FCSTD DOCUMENT  (FreeCAD 0.15R4671 (Git))
Label: Robot1c
License: All rights reserved
LicenseURL: http://en.wikipedia.org/wiki/All_rights_reserved
objects: Part::Part2DObjectPython×50, App::DocumentObjectGroup×10, Part::Feature×1
note: 51 computed .brp shape members not serialized (recipe doc carries the construction recipe); baked Part::Feature solids carry a one-line shape summary decoded from their .brp

FEATURE [Part::Part2DObjectPython] BSpline  label="BSpline Top"  # Draft 2D object (typed FeaturePython)
  Closed = false
  MakeFace = true
  Placement = pos=(0,20,0) rot=(0,0,1;0rad)
  Points = (3) [(-50,50,0),(0,60,0),(50,50,0)]
FEATURE [Part::Part2DObjectPython] BSpline001  label="BSpline Bottom"  # Draft 2D object (typed FeaturePython)
  Closed = false
  MakeFace = true
  Placement = pos=(0,-20,0) rot=(0,0,1;0rad)
  Points = (3) [(-50,-50,0),(0,-60,0),(50,-50,0)]
FEATURE [Part::Part2DObjectPython] Line  label="Line Left"  # Draft 2D object (typed FeaturePython)
  ChamferSize = 0
  Closed = false
  End = (-50,-70,0)
  FilletRadius = 0
  Length = 140
  MakeFace = false
  Points = (2) [(-50,70,0),(-50,-70,0)]
  Start = (-50,70,0)
FEATURE [Part::Part2DObjectPython] Line001  label="Line Right"  # Draft 2D object (typed FeaturePython)
  ChamferSize = 0
  Closed = false
  End = (50,-70,0)
  FilletRadius = 0
  Length = 140
  MakeFace = false
  Points = (2) [(50,70,0),(50,-70,0)]
  Start = (50,70,0)
FEATURE [Part::Part2DObjectPython] Circle  label="Upper Hole NW"  # Draft 2D object (typed FeaturePython)
  FirstAngle = 0
  LastAngle = 0
  MakeFace = false
  Placement = pos=(-80,57,0) rot=(0,0,1;0rad)
  Radius = 1.5
FEATURE [Part::Part2DObjectPython] Circle001  label="Lower Hole NW"  # Draft 2D object (typed FeaturePython)
  FirstAngle = 0
  LastAngle = 0
  MakeFace = false
  Placement = pos=(-80,40,0) rot=(0,0,1;0rad)
  Radius = 1.5
FEATURE [Part::Part2DObjectPython] Circle002  label="Upper Hole NE"  # Draft 2D object (typed FeaturePython)
  FirstAngle = 0
  LastAngle = 0
  MakeFace = false
  Placement = pos=(80,57,0) rot=(0,0,1;0rad)
  Radius = 1.5
FEATURE [Part::Part2DObjectPython] Circle003  label="Lower Hole NE"  # Draft 2D object (typed FeaturePython)
  FirstAngle = 0
  LastAngle = 0
  MakeFace = false
  Placement = pos=(80,40,0) rot=(0,0,1;0rad)
  Radius = 1.5
FEATURE [Part::Part2DObjectPython] DWire  label="Bracket Line NE"  # Draft 2D object (typed FeaturePython)
  ChamferSize = 0
  Closed = true
  End = (65,68,0)
  FilletRadius = 0
  Length = 123.985
  MakeFace = false
  Placement = pos=(145,2,0) rot=(0,0,1;0rad)
  Points = (8) [(-79.946,60.961,0),(-71,61,0),(-71,34,0),(-59,34,0),(-59,61,0),(-50,61,0),(-50,66,0),(-80,66,0)]
  Start = (65.054,62.961,0)
FEATURE [Part::Part2DObjectPython] Circle004  label="Upper Hole SW"  # Draft 2D object (typed FeaturePython)
  FirstAngle = 0
  LastAngle = 0
  MakeFace = false
  Placement = pos=(-60,-72,0) rot=(0,0,1;3.14159rad)
  Radius = 1.5
FEATURE [Part::Part2DObjectPython] Circle005  label="Lower Hole SW"  # Draft 2D object (typed FeaturePython)
  FirstAngle = 0
  LastAngle = 0
  MakeFace = false
  Placement = pos=(-60,-55,0) rot=(0,0,1;3.14159rad)
  Radius = 1.5
FEATURE [Part::Part2DObjectPython] DWire002  label="Bracket Line SW"  # Draft 2D object (typed FeaturePython)
  ChamferSize = 0
  Closed = true
  End = (-45,-83,0)
  FilletRadius = 0
  Length = 124
  MakeFace = false
  Placement = pos=(-125,-17,0) rot=(0,0,1;3.14159rad)
  Points = (8) [(-80,61,0),(-71,61,0),(-71,34,0),(-59,34,0),(-59,61,0),(-50,61,0),(-50,66,0),(-80,66,0)]
  Start = (-45,-78,0)
FEATURE [Part::Part2DObjectPython] Circle006  label="Upper Hole SE"  # Draft 2D object (typed FeaturePython)
  FirstAngle = 0
  LastAngle = 0
  MakeFace = false
  Placement = pos=(60,-72,0) rot=(0,0,1;3.14159rad)
  Radius = 1.5
FEATURE [Part::Part2DObjectPython] Circle007  label="Lower Hole SE"  # Draft 2D object (typed FeaturePython)
  FirstAngle = 0
  LastAngle = 0
  MakeFace = false
  Placement = pos=(60,-55,0) rot=(0,0,1;3.14159rad)
  Radius = 1.5
FEATURE [Part::Part2DObjectPython] DWire003  label="Bracket Line SE"  # Draft 2D object (typed FeaturePython)
  ChamferSize = 0
  Closed = true
  End = (75,-83,0)
  FilletRadius = 0
  Length = 124
  MakeFace = false
  Placement = pos=(-5,-17,0) rot=(0,0,1;3.14159rad)
  Points = (8) [(-80,61,0),(-71,61,0),(-71,34,0),(-59,34,0),(-59,61,0),(-50,61,0),(-50,66,0),(-80,66,0)]
  Start = (75,-78,0)
FEATURE [Part::Part2DObjectPython] Rectangle  label="Left Edge"  # Draft 2D object (typed FeaturePython)
  ChamferSize = 0
  FilletRadius = 0
  Height = -12
  Length = 3
  MakeFace = false
  Placement = pos=(-50,0,0) rot=(0,0,1;0rad)
FEATURE [Part::Part2DObjectPython] Rectangle001  label="Right Edge"  # Draft 2D object (typed FeaturePython)
  ChamferSize = 0
  FilletRadius = 0
  Height = -12
  Length = 3
  MakeFace = false
  Placement = pos=(47,0,0) rot=(0,0,1;0rad)
FEATURE [Part::Part2DObjectPython] Rectangle002  label="Left Inner Slot"  # Draft 2D object (typed FeaturePython)
  ChamferSize = 0
  FilletRadius = 0
  Height = -12
  Length = 3
  MakeFace = false
  Placement = pos=(-28,0,0) rot=(0,0,1;0rad)
FEATURE [Part::Part2DObjectPython] Rectangle003  label="Right Inner Slot"  # Draft 2D object (typed FeaturePython)
  ChamferSize = 0
  FilletRadius = 0
  Height = -12
  Length = 3
  MakeFace = false
  Placement = pos=(25.1317,0.340284,0) rot=(0,0,1;0rad)
FEATURE [Part::Part2DObjectPython] Circle008  label="Rim"  # Draft 2D object (typed FeaturePython)
  FirstAngle = 0
  LastAngle = 0
  MakeFace = false
  Placement = pos=(-85,0,0) rot=(0,0,1;0rad)
  Radius = 30
FEATURE [App::DocumentObjectGroup] Group001  label="Bracket SE"
  Group = -> [Circle006,Circle007,DWire003]
FEATURE [App::DocumentObjectGroup] Group002  label="Bracket SW"
  Group = -> [Circle004,Circle005,DWire002]
FEATURE [Part::Part2DObjectPython] Rectangle004  label="Axle hole"  # Draft 2D object (typed FeaturePython)
  ChamferSize = 0
  FilletRadius = 0
  Height = 3.5
  Length = 5.5
  MakeFace = false
  Placement = pos=(-87.75,-1.75,0) rot=(0,0,1;0rad)
FEATURE [Part::Part2DObjectPython] DWire004  label="Spoke Right"  # Draft 2D object (typed FeaturePython)
  ChamferSize = 0
  Closed = true
  End = (-76,2,0)
  FilletRadius = 0
  Length = 52.8444
  MakeFace = false
  Points = (4) [(-76,-2,0),(-64,-10,0),(-64,10,0),(-76,2,0)]
  Start = (-76,-2,0)
FEATURE [Part::Part2DObjectPython] DWire005  label="Spoke Bottom"  # Draft 2D object (typed FeaturePython)
  ChamferSize = 0
  Closed = true
  End = (-83,-7,0)
  FilletRadius = 0
  Length = 52.8444
  MakeFace = false
  Placement = pos=(-85,-83,0) rot=(0,0,-1;1.5708rad)
  Points = (4) [(-76,-2,0),(-64,-10,0),(-64,10,0),(-76,2,0)]
  Start = (-87,-7,0)
FEATURE [Part::Part2DObjectPython] DWire006  label="Spoke Top"  # Draft 2D object (typed FeaturePython)
  ChamferSize = 0
  Closed = true
  End = (-87,7,0)
  FilletRadius = 0
  Length = 52.8444
  MakeFace = false
  Placement = pos=(-85,83,0) rot=(0,0,1;1.5708rad)
  Points = (4) [(-76,-2,0),(-64,-10,0),(-64,10,0),(-76,2,0)]
  Start = (-83,7,0)
FEATURE [Part::Part2DObjectPython] DWire007  label="Spoke Left"  # Draft 2D object (typed FeaturePython)
  ChamferSize = 0
  Closed = true
  End = (-94,-2,0)
  FilletRadius = 0
  Length = 52.8444
  MakeFace = false
  Placement = pos=(-170,0,0) rot=(0,0,1;3.14159rad)
  Points = (4) [(-76,-2,0),(-64,-10,0),(-64,10,0),(-76,2,0)]
  Start = (-94,2,0)
FEATURE [App::DocumentObjectGroup] Group  label="Wheel Left"
  Group = -> [Circle008,Rectangle004,DWire004,DWire005,DWire006,DWire007]
FEATURE [Part::Part2DObjectPython] Circle009  label="Rim001"  # Draft 2D object (typed FeaturePython)
  FirstAngle = 0
  LastAngle = 0
  MakeFace = false
  Placement = pos=(85.1419,0,0) rot=(0,0,1;0rad)
  Radius = 30
FEATURE [Part::Part2DObjectPython] Rectangle005  label="Axle hole001"  # Draft 2D object (typed FeaturePython)
  ChamferSize = 0
  FilletRadius = 0
  Height = 3.5
  Length = 5.5
  MakeFace = false
  Placement = pos=(82.3919,-1.75,0) rot=(0,0,1;0rad)
FEATURE [Part::Part2DObjectPython] DWire008  label="Spoke Top001"  # Draft 2D object (typed FeaturePython)
  ChamferSize = 0
  Closed = true
  End = (83.1419,7,0)
  FilletRadius = 0
  Length = 52.8444
  MakeFace = false
  Placement = pos=(85.1419,83,0) rot=(0,0,1;1.5708rad)
  Points = (4) [(-76,-2,0),(-64,-10,0),(-64,10,0),(-76,2,0)]
  Start = (87.1419,7,0)
FEATURE [Part::Part2DObjectPython] DWire009  label="Spoke Right001"  # Draft 2D object (typed FeaturePython)
  ChamferSize = 0
  Closed = true
  End = (94.1419,2,0)
  FilletRadius = 0
  Length = 52.8444
  MakeFace = false
  Placement = pos=(170.142,0,0) rot=(0,0,1;0rad)
  Points = (4) [(-76,-2,0),(-64,-10,0),(-64,10,0),(-76,2,0)]
  Start = (94.1419,-2,0)
FEATURE [Part::Part2DObjectPython] DWire010  label="Spoke Bottom001"  # Draft 2D object (typed FeaturePython)
  ChamferSize = 0
  Closed = true
  End = (87.1419,-7,0)
  FilletRadius = 0
  Length = 52.8444
  MakeFace = false
  Placement = pos=(85.1419,-83,0) rot=(0,0,-1;1.5708rad)
  Points = (4) [(-76,-2,0),(-64,-10,0),(-64,10,0),(-76,2,0)]
  Start = (83.1419,-7,0)
FEATURE [Part::Part2DObjectPython] DWire011  label="Spoke Left001"  # Draft 2D object (typed FeaturePython)
  ChamferSize = 0
  Closed = true
  End = (76.1419,-2,0)
  FilletRadius = 0
  Length = 52.8444
  MakeFace = false
  Placement = pos=(0.141922,0,0) rot=(0,0,1;3.14159rad)
  Points = (4) [(-76,-2,0),(-64,-10,0),(-64,10,0),(-76,2,0)]
  Start = (76.1419,2,0)
FEATURE [App::DocumentObjectGroup] Group003  label="Wheel Right"
  Group = -> [Circle009,Rectangle005,DWire009,DWire010,DWire008,DWire011]
FEATURE [Part::Part2DObjectPython] Rectangle006  label="Axle Hub Hole"  # Draft 2D object (typed FeaturePython)
  ChamferSize = 0
  FilletRadius = 0
  Height = 3.5
  Length = 5.5
  MakeFace = false
  Placement = pos=(-89.4396,-84.0634,0) rot=(0,0,1;0rad)
FEATURE [Part::Part2DObjectPython] Circle010  label="Axle Circle Hub"  # Draft 2D object (typed FeaturePython)
  FirstAngle = 0
  LastAngle = 0
  MakeFace = false
  Placement = pos=(-86.6896,-82.3134,0) rot=(0,0,1;0rad)
  Radius = 5.71642
FEATURE [App::DocumentObjectGroup] Group004  label="Axle Hub Left"
  Group = -> [Rectangle006,Circle010]
FEATURE [Part::Part2DObjectPython] Rectangle007  label="Axle Hub Hole001"  # Draft 2D object (typed FeaturePython)
  ChamferSize = 0
  FilletRadius = 0
  Height = 3.5
  Length = 5.5
  MakeFace = false
  Placement = pos=(83.462,-84.0371,0) rot=(0,0,1;0rad)
FEATURE [Part::Part2DObjectPython] Circle011  label="Axle Circle Hub001"  # Draft 2D object (typed FeaturePython)
  FirstAngle = 0
  LastAngle = 0
  MakeFace = false
  Placement = pos=(86.212,-82.2871,0) rot=(0,0,1;0rad)
  Radius = 5.71642
FEATURE [App::DocumentObjectGroup] Group005  label="Axle Hub Right"
  Group = -> [Rectangle007,Circle011]
FEATURE [Part::Part2DObjectPython] Rectangle008  label="Left Wire Slot"  # Draft 2D object (typed FeaturePython)
  ChamferSize = 0
  FilletRadius = 0
  Height = -12
  Length = 3
  MakeFace = false
  Placement = pos=(-27.6597,25.8616,0) rot=(0,0,1;0rad)
FEATURE [Part::Part2DObjectPython] Rectangle009  label="Right Wire Slot"  # Draft 2D object (typed FeaturePython)
  ChamferSize = 0
  FilletRadius = 0
  Height = -12
  Length = 3
  MakeFace = false
  Placement = pos=(24.7441,26.2019,0) rot=(0,0,1;0rad)
FEATURE [Part::Part2DObjectPython] Circle012  label="Front Wheel Hole Right"  # Draft 2D object (typed FeaturePython)
  FirstAngle = 0
  LastAngle = 0
  MakeFace = false
  Placement = pos=(7.35,-95,0) rot=(0,0,1;0rad)
  Radius = 1.13
FEATURE [App::DocumentObjectGroup] Group006  label="Bracket NW"
  Group = -> [Circle,Circle001]
FEATURE [App::DocumentObjectGroup] Group007  label="Bracket NE"
  Group = -> [Circle002,Circle003,DWire]
FEATURE [Part::Part2DObjectPython] Circle013  label="Front Wheel Hole Left"  # Draft 2D object (typed FeaturePython)
  FirstAngle = 0
  LastAngle = 0
  MakeFace = false
  Placement = pos=(-7.35,-95,0) rot=(0,0,1;0rad)
  Radius = 1.13
FEATURE [Part::Feature] Wire
  Placement = pos=(-15,2,0) rot=(0,0,1;0rad)
  shape: bbox 30 x 32 x 2e-07 mm, 0 faces, 0 solids (baked)
FEATURE [Part::Part2DObjectPython] Rectangle010  label="Left Trike Slot"  # Draft 2D object (typed FeaturePython)
  ChamferSize = 0
  FilletRadius = 0
  Height = -12
  Length = 3
  MakeFace = false
  Placement = pos=(-20,70,0) rot=(0,0,1;0rad)
FEATURE [Part::Part2DObjectPython] Rectangle011  label="Right Trike Slot"  # Draft 2D object (typed FeaturePython)
  ChamferSize = 0
  FilletRadius = 0
  Height = -12
  Length = 3
  MakeFace = false
  Placement = pos=(17,70,0) rot=(0,0,1;0rad)
FEATURE [App::DocumentObjectGroup] Construction  label="Base Plate"
  Group = -> [Rectangle,Rectangle001,Line,Line001,BSpline,BSpline001,Rectangle002,Rectangle003,Rectangle008,Rectangle009,Rectangle010,Rectangle011]
FEATURE [Part::Part2DObjectPython] DWire012  label="Trike Side 1"  # Draft 2D object (typed FeaturePython)
  ChamferSize = 0
  Closed = true
  End = (-93,-70,0)
  FilletRadius = 0
  Length = 102.8
  MakeFace = false
  Points = (12) [(-93,-40,0),(-90.8,-40,0),(-90.8,-37.3,0),(-79.2,-37.3,0),(-79.2,-40,0),(-77,-40,0),(-77,-70,0),(-79.2,-70,0),(-79.2,-72.7,0),(-90.8,-72.7,0),(-90.8,-70,0),(-93,-70,0)]
  Start = (-93,-40,0)
FEATURE [Part::Part2DObjectPython] DWire013  label="Trike Side 2"  # Draft 2D object (typed FeaturePython)
  ChamferSize = 0
  Closed = true
  End = (77,-70,0)
  FilletRadius = 0
  Length = 102.8
  MakeFace = false
  Placement = pos=(170,0,0) rot=(0,0,1;0rad)
  Points = (12) [(-93,-40,0),(-90.8,-40,0),(-90.8,-37.3,0),(-79.2,-37.3,0),(-79.2,-40,0),(-77,-40,0),(-77,-70,0),(-79.2,-70,0),(-79.2,-72.7,0),(-90.8,-72.7,0),(-90.8,-70,0),(-93,-70,0)]
  Start = (77,-40,0)
FEATURE [Part::Part2DObjectPython] Rectangle012  label="Trike Base Rectangle"  # Draft 2D object (typed FeaturePython)
  ChamferSize = 0
  FilletRadius = 0
  Height = -20
  Length = -48
  MakeFace = false
  Placement = pos=(24,-85,0) rot=(0,0,1;0rad)
FEATURE [Part::Part2DObjectPython] Rectangle013  label="Right Trike Slot001"  # Draft 2D object (typed FeaturePython)
  ChamferSize = 0
  FilletRadius = 0
  Height = -12
  Length = 3
  MakeFace = false
  Placement = pos=(17,-89,0) rot=(0,0,1;0rad)
FEATURE [Part::Part2DObjectPython] Rectangle014  label="Left Trike Slot001"  # Draft 2D object (typed FeaturePython)
  ChamferSize = 0
  FilletRadius = 0
  Height = -12
  Length = 3
  MakeFace = false
  Placement = pos=(-20,-89,0) rot=(0,0,1;0rad)
FEATURE [App::DocumentObjectGroup] Group008  label="Trike Base Plate"
  Group = -> [Rectangle012,Circle012,Circle013,Rectangle013,Rectangle014]
FEATURE [Part::Part2DObjectPython] DWire014  label="Brace 1"  # Draft 2D object (typed FeaturePython)
  ChamferSize = 0
  Closed = true
  End = (-60,-40,0)
  FilletRadius = 0
  Length = 34.1421
  MakeFace = false
  Points = (3) [(-70,-30,0),(-70,-40,0),(-60,-40,0)]
  Start = (-70,-30,0)
FEATURE [Part::Part2DObjectPython] DWire015  label="Brace 2"  # Draft 2D object (typed FeaturePython)
  ChamferSize = 0
  Closed = true
  End = (70,-40,0)
  FilletRadius = 0
  Length = 34.1421
  MakeFace = false
  Placement = pos=(130,0,0) rot=(0,0,1;0rad)
  Points = (3) [(-70,-30,0),(-70,-40,0),(-60,-40,0)]
  Start = (60,-30,0)
FEATURE [Part::Part2DObjectPython] DWire016  label="Brace 3"  # Draft 2D object (typed FeaturePython)
  ChamferSize = 0
  Closed = true
  End = (-55,40,0)
  FilletRadius = 0
  Length = 34.1421
  MakeFace = false
  Placement = pos=(5,80,0) rot=(0,0,1;0rad)
  Points = (3) [(-70,-30,0),(-70,-40,0),(-60,-40,0)]
  Start = (-65,50,0)
FEATURE [Part::Part2DObjectPython] DWire017  label="Brace 4"  # Draft 2D object (typed FeaturePython)
  ChamferSize = 0
  Closed = true
  End = (66,40,0)
  FilletRadius = 0
  Length = 34.1421
  MakeFace = false
  Placement = pos=(126,80,0) rot=(0,0,1;0rad)
  Points = (3) [(-70,-30,0),(-70,-40,0),(-60,-40,0)]
  Start = (56,50,0)
